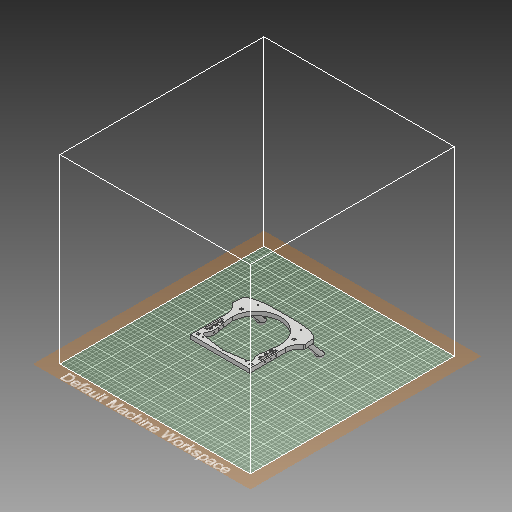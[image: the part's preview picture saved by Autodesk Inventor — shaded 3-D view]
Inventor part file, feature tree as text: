
AUTODESK INVENTOR PART (.ipt)
format: ipt  version: 2019 (Build 230136000, 136)  size: 1,055,744 bytes
history: native  units: mm
features: sketch x19, extrude x13, other x6, mirror x6, projected_geometry x5, revolve x1, loft x1, fillet x1
ambient origin geometry x8: Origin, YZ Plane, XZ Plane, XY Plane, X Axis, Y Axis, Z Axis, Center Point
bodies: Body1 (feature_tree)
feature tree (52):
  other  "Bryła1"
  extrude  "Wyciągnięcie proste1"  Depth=30.0mm
  sketch  "Szkic3"
  extrude  "Wyciągnięcie proste2"  Depth=65.0mm
  extrude  "Wyciągnięcie proste3"  Depth=9.0mm TaperAngle=0.0deg
  extrude  "Wyciągnięcie proste4"  Depth=3.0mm
  extrude  "Wyciągnięcie proste5"  Depth=3.0mm
  other  "Płaszczyzna konstrukcyjna1"
  mirror  "Odbij1"
  sketch  "Szkic7"
  extrude  "Wyciągnięcie proste6"  Depth=3.0mm
  extrude  "Wyciągnięcie proste7"  Depth=3.0mm
  extrude  "Wyciągnięcie proste8"  Depth=160.0mm
  mirror  "Odbij2"
  sketch  "Szkic9"
  other  "Płaszczyzna konstrukcyjna3"
  other  "Płaszczyzna konstrukcyjna5"
  revolve  "Obrót1"
  loft  "Wyciągnięcie złożone2"
  mirror  "Odbij3"
  extrude  "Wyciągnięcie proste9"  Depth=9.0mm TaperAngle=0.0deg
  mirror  "Odbij4"
  sketch  "Szkic14"
  extrude  "Wyciągnięcie proste10"  Depth=9.0mm TaperAngle=0.0deg
  mirror  "Odbij5"
  extrude  "Wyciągnięcie proste11"  Depth=6.0mm
  fillet  "Zaokrąglenie2"  Radius=3.0mm
  sketch  "Szkic17"
  sketch  "Szkic18"
  sketch  "Szkic19"
  sketch  "Szkic20"
  other  "Płaszczyzna konstrukcyjna6"
  extrude  "Wyciągnięcie proste12"  Depth=12.5mm
  extrude  "Wyciągnięcie proste13"  Depth=3.0mm
  mirror  "Odbij6"
  sketch  "Szkic2"
  sketch  "Szkic4"
  sketch  "Szkic5"
  sketch  "Szkic6"
  sketch  "Szkic8"
  projected_geometry  "Pętla rzutowana1"
  sketch  "Szkic12"
  other  "Krawędzie1"
  sketch  "Szkic13"
  projected_geometry  "Pętla rzutowana3"
  projected_geometry  "Pętla rzutowana4"
  sketch  "Szkic15"
  projected_geometry  "Pętla rzutowana5"
  sketch  "Szkic16"
  sketch  "Szkic21"
  sketch  "Szkic22"
  projected_geometry  "Pętla rzutowana6"
